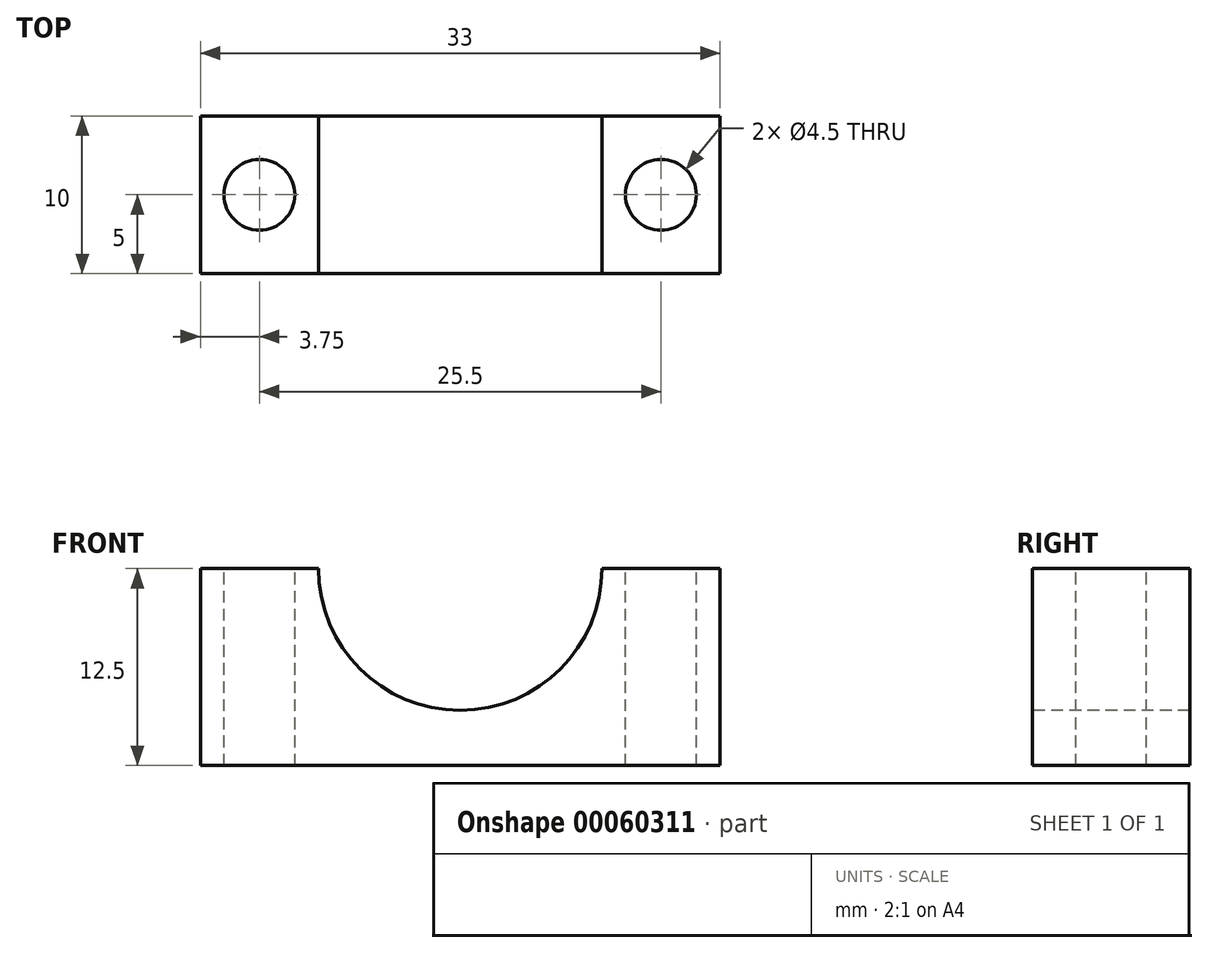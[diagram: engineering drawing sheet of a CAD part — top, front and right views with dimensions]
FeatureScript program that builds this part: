
annotation { "Feature Type Name" : "Feature", "Feature Type Description" : "" }
export const myFeature = defineFeature(function(context is Context, id is Id, definition is map)
    precondition{}
    {
        {
            var Q0;
            Q0=qCreatedBy(makeId("Top.planeOp"),FACE);
            var sketch = newSketch(context, id + "F0", { "sketchPlane" : qUnion([Q0])});
            skLineSegment(sketch, "E0.bottom", {"start": v(-16.5, 5) * mm, "end": v(16.5, 5) * mm});
            skLineSegment(sketch, "E0.top", {"start": v(-16.5, -5) * mm, "end": v(16.5, -5) * mm});
            skLineSegment(sketch, "E0.left", {"start": v(-16.5, 5) * mm, "end": v(-16.5, -5) * mm});
            skLineSegment(sketch, "E0.right", {"start": v(16.5, 5) * mm, "end": v(16.5, -5) * mm});
            skLineSegment(sketch, "E1", {"start": v(-16.5, 0) * mm, "end": v(16.5, 0) * mm, "construction": true});
            skPoint(sketch, "E1.startSnap0", {"position": v(-16.5, 0) * mm});
            skLineSegment(sketch, "E2", {"start": v(0, 5) * mm, "end": v(0, -5) * mm, "construction": true});
            skSolve(sketch);
        }
        {
            var Q0;
            Q0 = qSketchRegion(id + "F0", true);
            extrude(context, id + "F1", {"entities" : qUnion([Q0]), "depth" : 12.5 * mm});
        }
        {
            var Q0;
            Q0=makeQuery(id+"F1.opExtrude","SWEPT_FACE",FACE,{"disambiguationData":[OSD([sQuery(id+"F0.wireOp",EDGE,"E0.top")])]});
            var sketch = newSketch(context, id + "F2", { "sketchPlane" : qUnion([Q0])});
            skCircle(sketch, "E3", {"center": v(0, 12.5) * mm, "radius": 9 * mm});
            skSolve(sketch);
        }
        {
            var Q0;
            Q0 = qSketchRegion(id + "F2", true);
            extrude(context, id + "F3", {"entities" : qUnion([Q0]), "operationType" : NewBodyOperationType.REMOVE, "oppositeDirection" : true, "depth" : 10 * mm});
        }
        {
            var Q0;
            {var subQ0=sQuery(id+"F0.wireOp",EDGE,"E0.bottom");var subQ1=sQuery(id+"F0.wireOp",EDGE,"E0.top");var subQ2=sQuery(id+"F0.wireOp",EDGE,"E0.left");Q0=makeQuery(id+"F3.boolean.opBoolean","SPLIT",FACE,{"disambiguationData":[TD([makeQuery(id+"F1.opExtrude","SWEPT_FACE",FACE,{"disambiguationData":[OSD([subQ2])]})])],"derivedFrom":makeQuery(id+"F1.opExtrude","CAP_FACE",FACE,{"disambiguationData":[OSD([subQ0,subQ1,subQ2,sQuery(id+"F0.wireOp",EDGE,"E0.right")])],"isStart":false})});}
            var sketch = newSketch(context, id + "F4", { "sketchPlane" : qUnion([Q0])});
            skLineSegment(sketch, "E4", {"start": v(-16.5, 0) * mm, "end": v(16.56, 0) * mm, "construction": true});
            skPoint(sketch, "E4.endSnap0", {"position": v(-9, 0) * mm});
            skLineSegment(sketch, "E5", {"start": v(0, 0) * mm, "end": v(0, 4.76) * mm, "construction": true});
            skLineSegment(sketch, "E6", {"start": v(-12.75, 5) * mm, "end": v(-12.75, -5) * mm, "construction": true});
            skCircle(sketch, "E7", {"center": v(-12.75, 0) * mm, "radius": 2.25 * mm});
            skCircle(sketch, "E8.MirrorC", {"center": v(12.75, 0) * mm, "radius": 2.25 * mm});
            skSolve(sketch);
        }
        {
            var Q0;
            Q0 = qSketchRegion(id + "F4", true);
            extrude(context, id + "F5", {"entities" : qUnion([Q0]), "operationType" : NewBodyOperationType.REMOVE, "oppositeDirection" : true, "depth" : 12.5 * mm});
        }
    });
